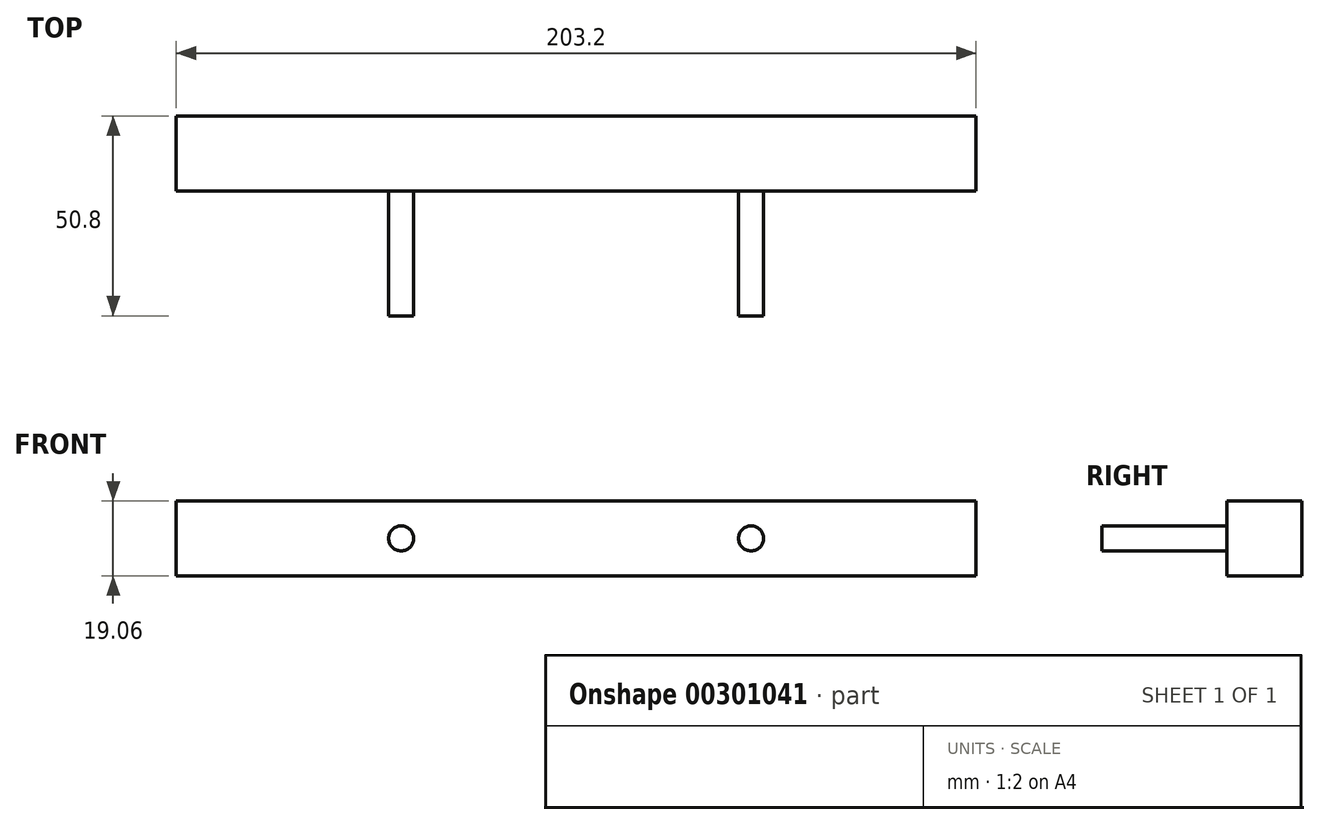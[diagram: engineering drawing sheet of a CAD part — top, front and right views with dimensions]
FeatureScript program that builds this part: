
annotation { "Feature Type Name" : "Feature", "Feature Type Description" : "" }
export const myFeature = defineFeature(function(context is Context, id is Id, definition is map)
    precondition{}
    {
        {
            var Q0;
            Q0=qCreatedBy(makeId("Front.planeOp"),FACE);
            var sketch = newSketch(context, id + "F0", { "sketchPlane" : qUnion([Q0])});
            skLineSegment(sketch, "E0.bottom", {"start": v(101.6, -9.52) * mm, "end": v(-101.6, -9.53) * mm});
            skLineSegment(sketch, "E0.top", {"start": v(101.6, 9.53) * mm, "end": v(-101.6, 9.52) * mm});
            skLineSegment(sketch, "E0.left", {"start": v(101.6, -9.52) * mm, "end": v(101.6, 9.53) * mm});
            skLineSegment(sketch, "E0.right", {"start": v(-101.6, -9.53) * mm, "end": v(-101.6, 9.52) * mm});
            skPoint(sketch, "E0.middle", {"position": v(0, 0) * mm});
            skSolve(sketch);
        }
        {
            var Q0;
            Q0 = qSketchRegion(id + "F0", true);
            extrude(context, id + "F1", {"entities" : qUnion([Q0]), "depth" : 19.05 * mm});
        }
        {
            var Q0;
            Q0=qCreatedBy(makeId("Front.planeOp"),FACE);
            var sketch = newSketch(context, id + "F2", { "sketchPlane" : qUnion([Q0])});
            skLineSegment(sketch, "E1", {"start": v(0, 0) * mm, "end": v(44.45, 0) * mm});
            skLineSegment(sketch, "E2", {"start": v(44.45, 0) * mm, "end": v(0, 0) * mm});
            skLineSegment(sketch, "E3", {"start": v(-44.45, 0) * mm, "end": v(0, 0) * mm});
            skCircle(sketch, "E4", {"center": v(-44.45, 0) * mm, "radius": 3.18 * mm});
            skCircle(sketch, "E5", {"center": v(44.45, 0) * mm, "radius": 3.18 * mm});
            skSolve(sketch);
        }
        {
            var Q0;
            Q0 = qSketchRegion(id + "F2", true);
            extrude(context, id + "F3", {"entities" : qUnion([Q0]), "operationType" : NewBodyOperationType.ADD, "depth" : 50.8 * mm});
        }
    });
